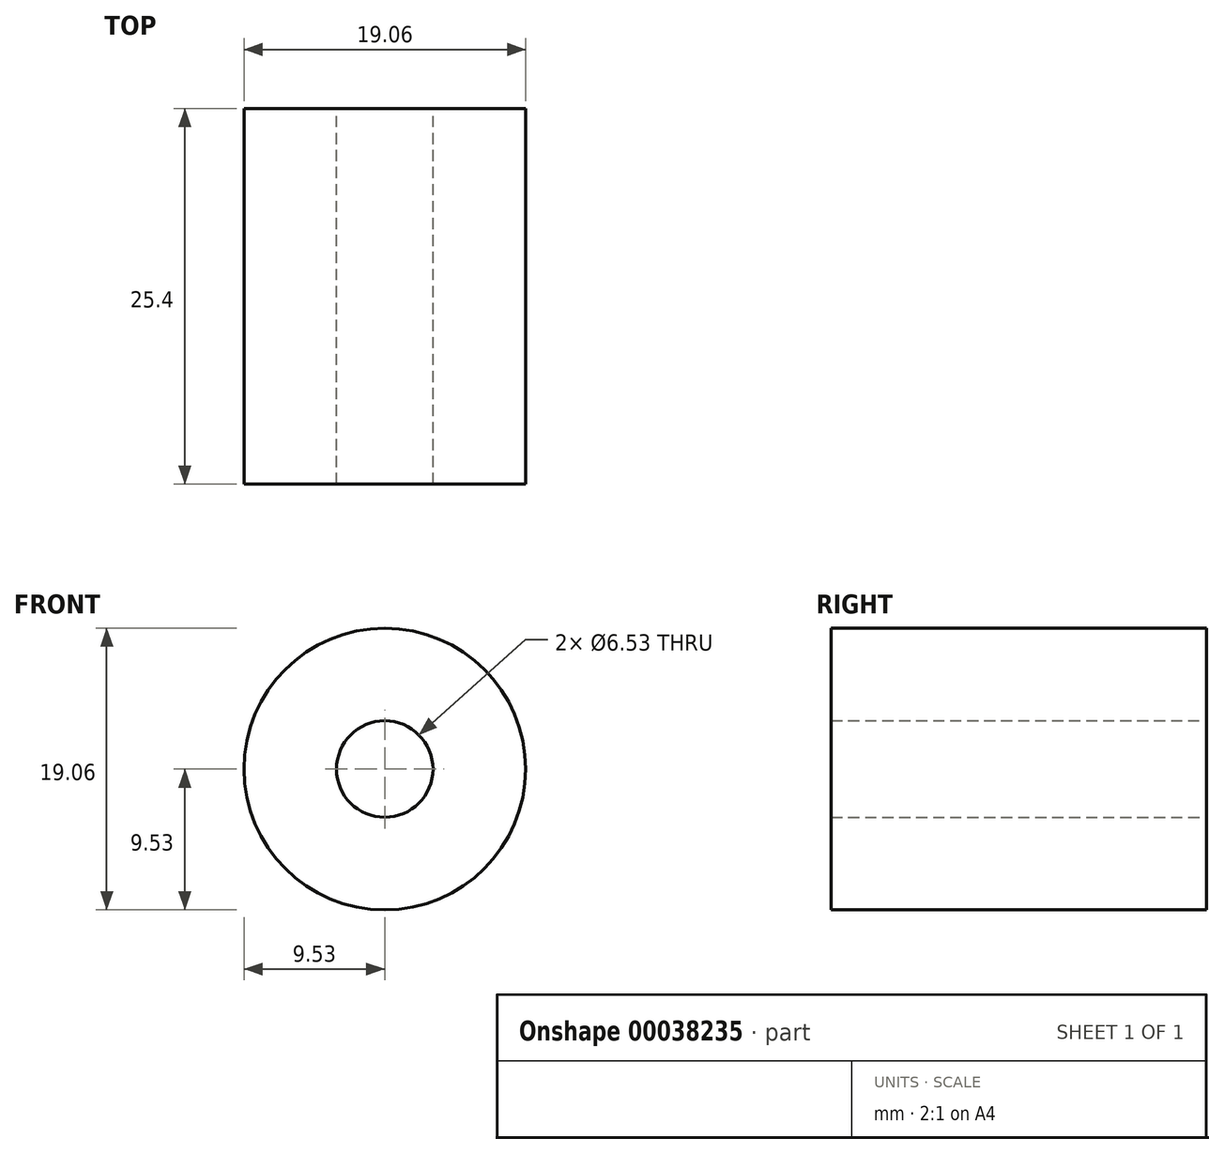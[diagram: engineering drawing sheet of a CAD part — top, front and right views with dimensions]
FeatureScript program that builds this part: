
annotation { "Feature Type Name" : "Feature", "Feature Type Description" : "" }
export const myFeature = defineFeature(function(context is Context, id is Id, definition is map)
    precondition{}
    {
        {
            var Q0;
            Q0=qCreatedBy(makeId("Front.planeOp"),FACE);
            var sketch = newSketch(context, id + "F0", { "sketchPlane" : qUnion([Q0])});
            skCircle(sketch, "E0", {"center": v(0, 0) * mm, "radius": 9.53 * mm});
            skCircle(sketch, "E1", {"center": v(0, 0) * mm, "radius": 3.26 * mm});
            skSolve(sketch);
        }
        {
            var Q0;
            Q0=makeQuery(id+"F0.imprint","IMPRINT",FACE,{"disambiguationData":[TD([[makeQuery(id+"F0.imprint","IMPRINT",EDGE,{"derivedFrom":sQuery(id+"F0.wireOp",EDGE,"E0")}),1.0]])]});
            extrude(context, id + "F1", {"entities" : qUnion([Q0]), "depth" : 25.4 * mm});
        }
    });
